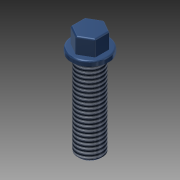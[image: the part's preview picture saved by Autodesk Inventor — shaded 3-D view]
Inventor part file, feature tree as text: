
AUTODESK INVENTOR PART (.ipt)
format: ipt  version: 2015 (Build 190159000, 159)  size: 133,120 bytes
history: native  units: mm
features: extrude x3, sketch x3, thread x1, chamfer x1, fillet x1
ambient origin geometry x8: Origin, YZ Plane, XZ Plane, XY Plane, X Axis, Y Axis, Z Axis, Center Point
bodies: 实体1 (feature_tree)
feature tree (9):
  extrude  "拉伸1"  Depth=1.5mm TaperAngle=0.0deg
  extrude  "拉伸2"  Depth=8.0mm
  extrude  "拉伸3"  Depth=8.0mm
  thread  "螺纹1"  [1 undecoded]
  chamfer  "倒角1"  Distance=10.0mm
  fillet  "圆角1"  Radius=0.5mm
  sketch  "草图1"  dims[d0=12.0mm d1=1.5mm d2=0.0mm]
  sketch  "草图2"  dims[d3=8.0mm d4=2.959103mm]
  sketch  "草图3"  dims[d5=5.0mm d6=0.0mm d7=8.0mm d8=28.0mm d9=0.0mm d10=10.0mm d11=0.0mm d12=0.5mm d13=2.0mm d14=45.0deg d15=0.5mm]
note: 1 required parameter value undecoded (feature->parameter linkage not recoverable at this tier; creation-order binding heuristic only, values carry confidence <= 0.55)
